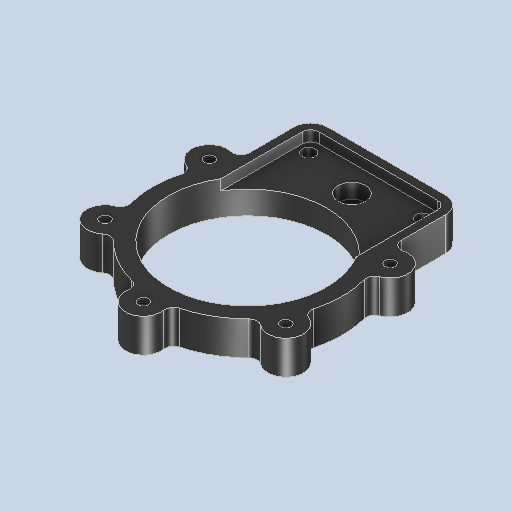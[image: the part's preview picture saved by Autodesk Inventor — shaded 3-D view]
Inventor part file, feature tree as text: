
AUTODESK INVENTOR PART (.ipt)
format: ipt  version: 2024.2 (Build 282272000, 272)  size: 322,560 bytes
history: native  units: mm
features: other x4, sketch x3, extrude x2, hole x2
ambient origin geometry x8: Origin, YZ Plane, XZ Plane, XY Plane, X Axis, Y Axis, Z Axis, Center Point
bodies: Solid1 (feature_tree)
feature tree (11):
  other  "CrossRollerBearingOuterSupportStand.ipt"
  sketch  "Sketch2"  dims[d4=2.459mm d5=6.0mm d6=6.5mm d7=3.5mm d8=90.0deg d9=8.0mm d10=20.594885mm d11=2.0mm]
  extrude  "Extrusion1"  Depth=8.0mm TaperAngle=0.0deg
  extrude  "Extrusion2"  Depth=2.0mm
  hole  "Phi3.1"  [1 undecoded]
  hole  "Phi3.5"  [1 undecoded]
  sketch  "Sketch1"  dims[d0=10.0mm d2=8.0mm d3=0.0mm]
  other  "TaggingFeature1"
  sketch  "Sketch3"  dims[d19=43.0mm d20=32.0mm d21=16.0mm d22=9.5mm d23=27.0mm d24=27.0mm d25=8.5mm d26=37.5mm d27=0.05mm d28=2.0mm d29=2.0mm d30=2.0mm d31=2.5mm d32=0.0mm d34=4.0mm d35=3.1mm d36=6.0mm d37=6.5mm d38=3.5mm d39=90.0deg d40=8.0mm d41=20.594885mm d42=3.5mm d43=6.0mm d44=6.5mm d45=3.5mm d46=90.0deg d47=8.8mm d48=0.0mm]
  other  "Solid1::CrossRollerBearingOuterSupportStand.ipt"
  other  "Srf2"
note: 2 required parameter values undecoded (feature->parameter linkage not recoverable at this tier; creation-order binding heuristic only, values carry confidence <= 0.55)
